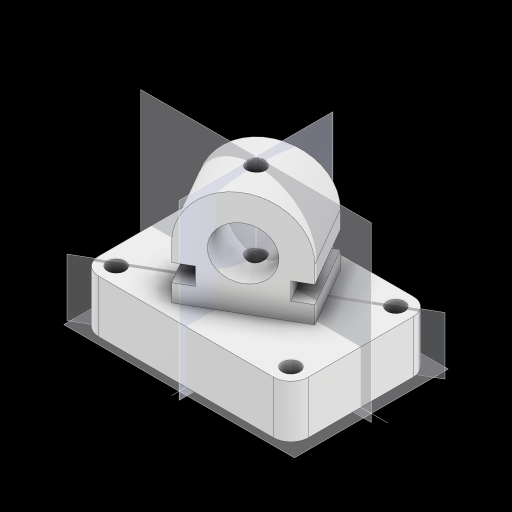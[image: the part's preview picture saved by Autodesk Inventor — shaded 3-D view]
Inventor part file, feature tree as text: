
AUTODESK INVENTOR PART (.ipt)
format: ipt  version: 2024 (Build 280153000, 153)  size: 209,408 bytes
history: native  units: in
note: dims shown in document units (in); Inventor stores cm internally (conversion verified against a paired STEP export)
features: sketch x3, extrude x2, plane x1, hole x1
ambient origin geometry x8: Origin, YZ Plane, XZ Plane, XY Plane, X Axis, Y Axis, Z Axis, Center Point
bodies: Solid1 (feature_tree)
feature tree (7):
  extrude  "Extrusion1"  Depth=0.25in
  plane  "Work Plane1"
  extrude  "Extrusion2"  Depth=2.0in
  hole  "Hole6"  [1 undecoded]
  sketch  "Sketch1"  dims[d0=0.25in d1=0.25in]
  sketch  "Sketch2"  dims[d2=3.0in d3=2.0in]
  sketch  "Sketch6"  dims[d4=1.5in d5=1.0in d6=0.75in d7=0.0in d8=30.0deg d9=0.75in d10=0.25in d11=0.25in d13=0.25in d14=0.25in d15=1.5in d17=0.75in d18=0.25in d19=0.25in d20=0.75in d21=1.0in d22=0.0in d67=0.25in d68=0.75in d69=0.375in d70=0.25in d71=0.5635in d72=1.0in d73=0.8108in d74=0.75in d75=0.8108in d76=0.0625in d77=0.75in d78=0.375in]
note: 1 required parameter value undecoded (feature->parameter linkage not recoverable at this tier; creation-order binding heuristic only, values carry confidence <= 0.55)
